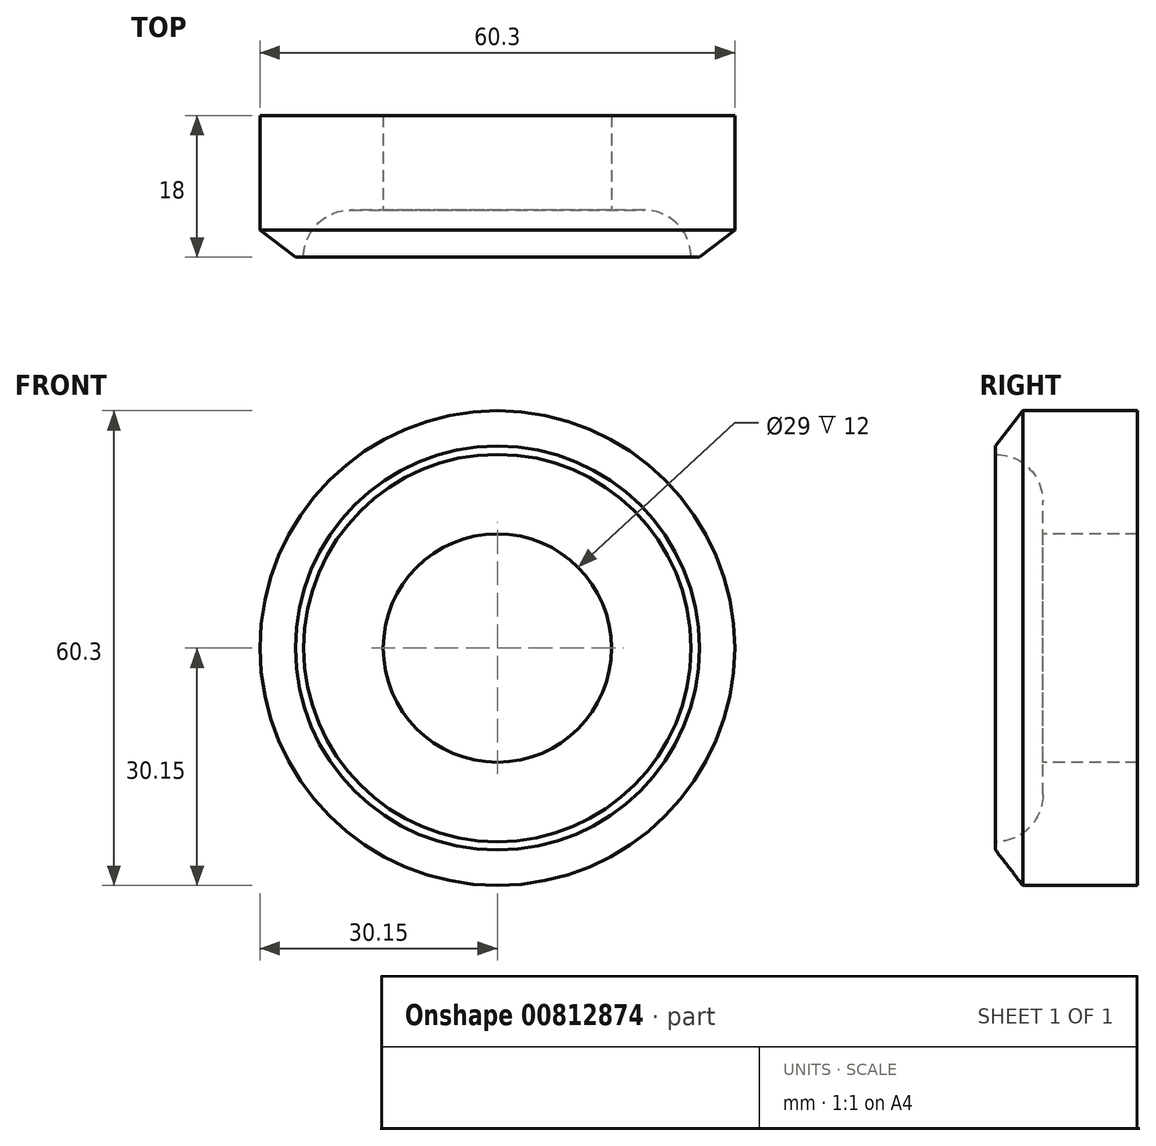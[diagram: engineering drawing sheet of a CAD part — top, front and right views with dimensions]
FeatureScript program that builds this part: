
annotation { "Feature Type Name" : "Feature", "Feature Type Description" : "" }
export const myFeature = defineFeature(function(context is Context, id is Id, definition is map)
    precondition{}
    {
        {
            var Q0;
            Q0=qCreatedBy(makeId("Front.planeOp"),FACE);
            var sketch = newSketch(context, id + "F0", { "sketchPlane" : qUnion([Q0])});
            skCircle(sketch, "E0", {"center": v(0, 0) * mm, "radius": 30.15 * mm});
            skSolve(sketch);
        }
        {
            var Q0;
            Q0 = qSketchRegion(id + "F0", true);
            extrude(context, id + "F1", {"entities" : qUnion([Q0]), "depth" : 18 * mm, "offsetDistance" : 25 * mm});
        }
        {
            var Q0;
            Q0=makeQuery(id+"F1.opExtrude","CAP_FACE",FACE,{"disambiguationData":[OSD([sQuery(id+"F0.wireOp",EDGE,"E0")])],"isStart":false});
            var sketch = newSketch(context, id + "F2", { "sketchPlane" : qUnion([Q0])});
            skCircle(sketch, "E1", {"center": v(0, 0) * mm, "radius": 24.6 * mm});
            skSolve(sketch);
        }
        {
            var Q0;
            Q0 = qSketchRegion(id + "F2", true);
            extrude(context, id + "F3", {"entities" : qUnion([Q0]), "operationType" : NewBodyOperationType.REMOVE, "oppositeDirection" : true, "depth" : 6 * mm, "offsetDistance" : 25 * mm});
        }
        {
            var Q0;
            Q0=makeQuery(id+"F3.boolean.opBoolean","COPY",EDGE,{"derivedFrom":makeQuery(id+"F3.opExtrude","CAP_EDGE",EDGE,{"disambiguationData":[OSD([sQuery(id+"F2.wireOp",EDGE,"E1")])],"isStart":false})});
            fillet(context, id + "F4", {"entities" : qUnion([Q0]), "radius" : 6 * mm, "tangentPropagation" : true, "allowEdgeOverflow" : false});
        }
        {
            var Q0;
            Q0=makeQuery(id+"F3.boolean.opBoolean","COPY",FACE,{"derivedFrom":makeQuery(id+"F3.opExtrude","CAP_FACE",FACE,{"disambiguationData":[OSD([sQuery(id+"F2.wireOp",EDGE,"E1")])],"isStart":false})});
            var sketch = newSketch(context, id + "F5", { "sketchPlane" : qUnion([Q0])});
            skCircle(sketch, "E2", {"center": v(0, 0) * mm, "radius": 14.5 * mm});
            skSolve(sketch);
        }
        {
            var Q0;
            Q0=makeQuery(id+"F5.imprint","IMPRINT",FACE,{"disambiguationData":[TD([[makeQuery(id+"F5.imprint","IMPRINT",EDGE,{"derivedFrom":sQuery(id+"F5.wireOp",EDGE,"E2")}),1.0]])]});
            extrude(context, id + "F6", {"entities" : qUnion([Q0]), "operationType" : NewBodyOperationType.REMOVE, "oppositeDirection" : true, "depth" : 25 * mm, "offsetDistance" : 25 * mm});
        }
        {
            var Q0;
            Q0=qCreatedBy(makeId("Top.planeOp"),FACE);
            var sketch = newSketch(context, id + "F7", { "sketchPlane" : qUnion([Q0])});
            skLineSegment(sketch, "E3", {"start": v(-25.66, -18) * mm, "end": v(-30.15, -14.55) * mm});
            skLineSegment(sketch, "E4", {"start": v(0, 0) * mm, "end": v(0, -4.5) * mm});
            skLineSegment(sketch, "E5", {"start": v(0, 0) * mm, "end": v(0, -18) * mm});
            skLineSegment(sketch, "E6", {"start": v(0, -18) * mm, "end": v(-30.15, -18) * mm});
            skLineSegment(sketch, "E7", {"start": v(-30.15, -18) * mm, "end": v(-30.15, -14.55) * mm});
            skSolve(sketch);
        }
        {
            var Q0;
            Q0 = qSketchRegion(id + "F7", true);
            var Q1;
            Q1=sQuery(id+"F7.wireOp",EDGE,"E4");
            revolve(context, id + "F8", {"operationType" : NewBodyOperationType.REMOVE, "surfaceOperationType" : NewSurfaceOperationType.NEW, "entities" : qUnion([Q0]), "axis" : qUnion([Q1]), "revolveType" : RevolveType.FULL, "oppositeDirection" : true});
        }
    });
